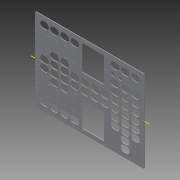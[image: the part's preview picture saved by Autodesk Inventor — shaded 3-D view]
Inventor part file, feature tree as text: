
AUTODESK INVENTOR PART (.ipt)
format: ipt  version: 2014 SP1 (Build 180222100, 222)  size: 889,344 bytes
history: native  units: in
note: dims shown in document units (in); Inventor stores cm internally (conversion verified against a paired STEP export)
features: reference x83, other x11, sketch x10, sheet_metal_op x5, pattern_linear x2, chamfer x1, plane x1, mirror x1, projected_geometry x1
ambient origin geometry x8: Origin, YZ Plane, XZ Plane, XY Plane, X Axis, Y Axis, Z Axis, Center Point
bodies: Solid1 (feature_tree)
feature tree (115):
  sheet_metal_op  "Face1"
  pattern_linear  "Rectangular Pattern2"  Count1=27 Spacing1=1.0in
  pattern_linear  "Rectangular Pattern5"  Spacing1=0.125in  [1 undecoded]
  sheet_metal_op  "Face4"
  sheet_metal_op  "Face5"
  sketch  "Sketch22"  dims[d18=0.0in d19=10.6299in d21=1.0in]
  chamfer  "Corner Round1"
  plane  "Work Plane1"
  mirror  "Mirror1"
  sketch  "Sketch1"  dims[d0=27.0in]
  other  "Plate1"
  sketch  "Sketch2"  dims[d1=20.325in]
  sketch  "Sketch4"  dims[d2=0.125in]
  reference  "Reference4"
  reference  "Reference5"
  sketch  "Sketch12"  dims[d4=7.25in]
  reference  "Reference10"
  reference  "Reference11"
  sketch  "Sketch16"  dims[d5=5.5in]
  reference  "Reference12"
  reference  "Reference13"
  reference  "Reference14"
  reference  "Reference15"
  reference  "Reference16"
  reference  "Reference17"
  reference  "Reference18"
  reference  "Reference19"
  reference  "Reference20"
  reference  "Reference21"
  reference  "Reference22"
  reference  "Reference23"
  reference  "Reference24"
  reference  "Reference25"
  reference  "Reference26"
  reference  "Reference27"
  reference  "Reference28"
  reference  "Reference29"
  reference  "Reference30"
  reference  "Reference31"
  reference  "Reference32"
  reference  "Reference33"
  reference  "Reference34"
  reference  "Reference35"
  reference  "Reference36"
  reference  "Reference37"
  reference  "Reference38"
  reference  "Reference39"
  reference  "Reference40"
  reference  "Reference41"
  reference  "Reference42"
  reference  "Reference43"
  reference  "Reference44"
  reference  "Reference45"
  reference  "Reference46"
  projected_geometry  "Projected Loop1"
  reference  "Reference47"
  reference  "Reference48"
  reference  "Reference49"
  reference  "Reference50"
  reference  "Reference51"
  reference  "Reference52"
  reference  "Reference53"
  reference  "Reference54"
  reference  "Reference55"
  reference  "Reference56"
  reference  "Reference57"
  reference  "Reference58"
  reference  "Reference59"
  reference  "Reference60"
  reference  "Reference61"
  reference  "Reference62"
  reference  "Reference63"
  reference  "Reference64"
  reference  "Reference65"
  reference  "Reference66"
  reference  "Reference67"
  reference  "Reference68"
  reference  "Reference69"
  reference  "Reference70"
  reference  "Reference71"
  reference  "Reference72"
  reference  "Reference73"
  reference  "Reference74"
  reference  "Reference75"
  reference  "Reference76"
  reference  "Reference77"
  reference  "Reference78"
  reference  "Reference79"
  reference  "Reference80"
  reference  "Reference81"
  reference  "Reference82"
  reference  "Reference83"
  reference  "Reference84"
  reference  "Reference85"
  reference  "Reference86"
  reference  "Reference87"
  reference  "Reference88"
  sketch  "Sketch19"  dims[d6=7.25in]
  other  "Plate4"
  sheet_metal_op  "Bend3"
  sketch  "Sketch21"  dims[d17=0.125in]
  other  "Plate5"
  sheet_metal_op  "Bend4"
  sketch  "Sketch24"  dims[d23=1.0in]
  reference  "Reference89"
  reference  "Reference90"
  sketch  "Sketch25"  dims[d24=1.0in d65=0.125in d66=0.0in d78=11.55in d79=5.5in d80=11.55in d97=0.125in d98=0.0in d99=7.4803in d101=1.0in d102=0.7874in d104=26.0in d105=0.125in d106=0.0in d107=1.0in d109=1.8325in d110=2.5in d111=0.125in d112=3.937in d114=1.8325in d115=3.937in d117=2.5in d122=0.125in d123=0.125in d124=0.0625in d125=0.25in d126=0.125in d127=0.125in d128=0.125in d129=0.0625in d130=0.25in d131=0.125in d132=0.25in d133=2.8579in d134=1.57in d135=2.29in d136=0.171in d137=0.171in d138=0.125in d139=0.0in d140=-10.1625in d141=1.75in d142=0.266in d143=4.5in d144=0.266in d145=0.125in d146=0.0in d147=1.0in d148=1.0in d149=0.125in d150=0.0in d151=0.125in d152=0.0in]
  other  "Cut3"
  other  "Cut6"
  other  "Cut8"
  other  "Cut9"
  other  "Cut11"
  other  "Cut12"
  other  "Cut13"
  other  "Cut14"
note: 1 required parameter value undecoded (feature->parameter linkage not recoverable at this tier; creation-order binding heuristic only, values carry confidence <= 0.55)
